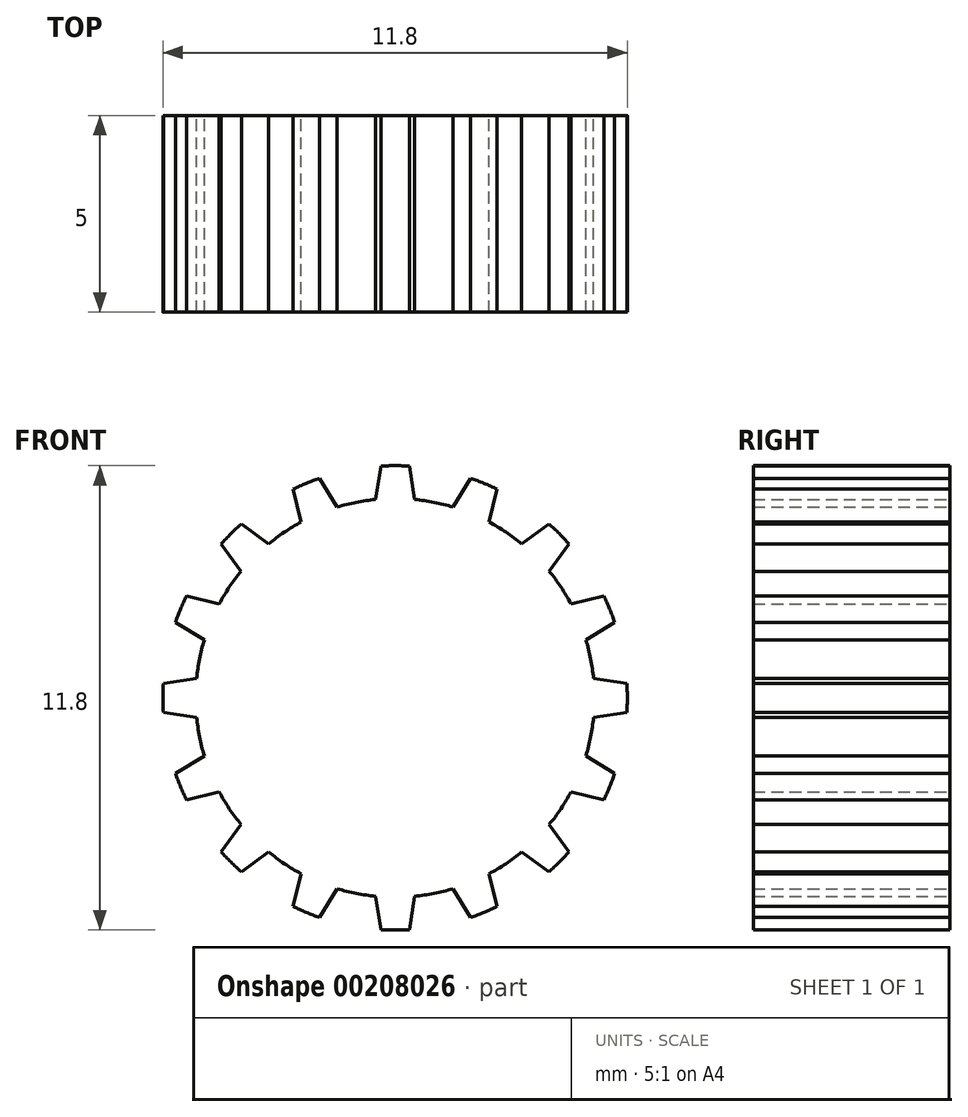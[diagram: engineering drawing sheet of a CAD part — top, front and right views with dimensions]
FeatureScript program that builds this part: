
annotation { "Feature Type Name" : "Feature", "Feature Type Description" : "" }
export const myFeature = defineFeature(function(context is Context, id is Id, definition is map)
    precondition{}
    {
        {
            var Q0;
            Q0=qCreatedBy(makeId("Front.planeOp"),FACE);
            var sketch = newSketch(context, id + "F0", { "sketchPlane" : qUnion([Q0])});
            skLineSegment(sketch, "E0", {"start": v(0, 0) * mm, "end": v(6.24, -1.24) * mm, "construction": true});
            skCircle(sketch, "E1", {"center": v(0, 0) * mm, "radius": 5.9 * mm, "construction": true});
            skCircle(sketch, "E2", {"center": v(0, 0) * mm, "radius": 5.07 * mm, "construction": true});
            skArc(sketch, "E3", {"start": v(4.97, -0.99) * mm, "mid": v(5.01, -0.74) * mm, "end": v(5.04, -0.5) * mm});
            skArc(sketch, "E4", {"start": v(5.9, 0) * mm, "mid": v(5.9, -0.18) * mm, "end": v(5.89, -0.36) * mm});
            skLineSegment(sketch, "E5", {"start": v(5.04, -0.5) * mm, "end": v(5.89, -0.36) * mm});
            skArc(sketch, "E6.MirrorCS", {"start": v(4.97, -0.99) * mm, "mid": v(4.91, -1.23) * mm, "end": v(4.85, -1.47) * mm});
            skLineSegment(sketch, "E7.MirrorCS", {"start": v(4.85, -1.47) * mm, "end": v(5.58, -1.92) * mm});
            skArc(sketch, "E8.MirrorCS", {"start": v(5.45, -2.26) * mm, "mid": v(5.52, -2.09) * mm, "end": v(5.58, -1.92) * mm});
            skArc(sketch, "E9.1.0", {"start": v(5.45, 2.26) * mm, "mid": v(5.52, 2.09) * mm, "end": v(5.58, 1.92) * mm});
            skLineSegment(sketch, "E9.1.1", {"start": v(4.85, 1.47) * mm, "end": v(5.58, 1.92) * mm});
            skArc(sketch, "E9.1.2", {"start": v(4.97, 0.99) * mm, "mid": v(4.91, 1.23) * mm, "end": v(4.85, 1.47) * mm});
            skArc(sketch, "E9.1.3", {"start": v(4.97, 0.99) * mm, "mid": v(5.01, 0.74) * mm, "end": v(5.04, 0.5) * mm});
            skLineSegment(sketch, "E9.1.4", {"start": v(5.04, 0.5) * mm, "end": v(5.89, 0.36) * mm});
            skArc(sketch, "E9.1.5", {"start": v(5.9, 0) * mm, "mid": v(5.9, 0.18) * mm, "end": v(5.89, 0.36) * mm});
            skArc(sketch, "E9.2.0", {"start": v(4.17, 4.17) * mm, "mid": v(4.3, 4.04) * mm, "end": v(4.42, 3.9) * mm});
            skLineSegment(sketch, "E9.2.1", {"start": v(3.91, 3.22) * mm, "end": v(4.42, 3.9) * mm});
            skArc(sketch, "E9.2.2", {"start": v(4.21, 2.81) * mm, "mid": v(4.07, 3.02) * mm, "end": v(3.91, 3.22) * mm});
            skArc(sketch, "E9.2.3", {"start": v(4.21, 2.81) * mm, "mid": v(4.35, 2.6) * mm, "end": v(4.47, 2.39) * mm});
            skLineSegment(sketch, "E9.2.4", {"start": v(4.47, 2.39) * mm, "end": v(5.3, 2.59) * mm});
            skArc(sketch, "E9.2.5", {"start": v(5.45, 2.26) * mm, "mid": v(5.38, 2.42) * mm, "end": v(5.3, 2.59) * mm});
            skArc(sketch, "E9.3.0", {"start": v(2.26, 5.45) * mm, "mid": v(2.42, 5.38) * mm, "end": v(2.59, 5.3) * mm});
            skLineSegment(sketch, "E9.3.1", {"start": v(2.39, 4.47) * mm, "end": v(2.59, 5.3) * mm});
            skArc(sketch, "E9.3.2", {"start": v(2.81, 4.21) * mm, "mid": v(2.6, 4.35) * mm, "end": v(2.39, 4.47) * mm});
            skArc(sketch, "E9.3.3", {"start": v(2.81, 4.21) * mm, "mid": v(3.02, 4.07) * mm, "end": v(3.22, 3.91) * mm});
            skLineSegment(sketch, "E9.3.4", {"start": v(3.22, 3.91) * mm, "end": v(3.9, 4.42) * mm});
            skArc(sketch, "E9.3.5", {"start": v(4.17, 4.17) * mm, "mid": v(4.04, 4.3) * mm, "end": v(3.9, 4.42) * mm});
            skArc(sketch, "E9.4.0", {"start": v(0, 5.9) * mm, "mid": v(0.18, 5.9) * mm, "end": v(0.36, 5.89) * mm});
            skLineSegment(sketch, "E9.4.1", {"start": v(0.5, 5.04) * mm, "end": v(0.36, 5.89) * mm});
            skArc(sketch, "E9.4.2", {"start": v(0.99, 4.97) * mm, "mid": v(0.74, 5.01) * mm, "end": v(0.5, 5.04) * mm});
            skArc(sketch, "E9.4.3", {"start": v(0.99, 4.97) * mm, "mid": v(1.23, 4.91) * mm, "end": v(1.47, 4.85) * mm});
            skLineSegment(sketch, "E9.4.4", {"start": v(1.47, 4.85) * mm, "end": v(1.92, 5.58) * mm});
            skArc(sketch, "E9.4.5", {"start": v(2.26, 5.45) * mm, "mid": v(2.09, 5.52) * mm, "end": v(1.92, 5.58) * mm});
            skArc(sketch, "E9.5.0", {"start": v(-2.26, 5.45) * mm, "mid": v(-2.09, 5.52) * mm, "end": v(-1.92, 5.58) * mm});
            skLineSegment(sketch, "E9.5.1", {"start": v(-1.47, 4.85) * mm, "end": v(-1.92, 5.58) * mm});
            skArc(sketch, "E9.5.2", {"start": v(-0.99, 4.97) * mm, "mid": v(-1.23, 4.91) * mm, "end": v(-1.47, 4.85) * mm});
            skArc(sketch, "E9.5.3", {"start": v(-0.99, 4.97) * mm, "mid": v(-0.74, 5.01) * mm, "end": v(-0.5, 5.04) * mm});
            skLineSegment(sketch, "E9.5.4", {"start": v(-0.5, 5.04) * mm, "end": v(-0.36, 5.89) * mm});
            skArc(sketch, "E9.5.5", {"start": v(0, 5.9) * mm, "mid": v(-0.18, 5.9) * mm, "end": v(-0.36, 5.89) * mm});
            skArc(sketch, "E9.6.0", {"start": v(-4.17, 4.17) * mm, "mid": v(-4.04, 4.3) * mm, "end": v(-3.9, 4.42) * mm});
            skLineSegment(sketch, "E9.6.1", {"start": v(-3.22, 3.91) * mm, "end": v(-3.9, 4.42) * mm});
            skArc(sketch, "E9.6.2", {"start": v(-2.81, 4.21) * mm, "mid": v(-3.02, 4.07) * mm, "end": v(-3.22, 3.91) * mm});
            skArc(sketch, "E9.6.3", {"start": v(-2.81, 4.21) * mm, "mid": v(-2.6, 4.35) * mm, "end": v(-2.39, 4.47) * mm});
            skLineSegment(sketch, "E9.6.4", {"start": v(-2.39, 4.47) * mm, "end": v(-2.59, 5.3) * mm});
            skArc(sketch, "E9.6.5", {"start": v(-2.26, 5.45) * mm, "mid": v(-2.42, 5.38) * mm, "end": v(-2.59, 5.3) * mm});
            skArc(sketch, "E9.7.0", {"start": v(-5.45, 2.26) * mm, "mid": v(-5.38, 2.42) * mm, "end": v(-5.3, 2.59) * mm});
            skLineSegment(sketch, "E9.7.1", {"start": v(-4.47, 2.39) * mm, "end": v(-5.3, 2.59) * mm});
            skArc(sketch, "E9.7.2", {"start": v(-4.21, 2.81) * mm, "mid": v(-4.35, 2.6) * mm, "end": v(-4.47, 2.39) * mm});
            skArc(sketch, "E9.7.3", {"start": v(-4.21, 2.81) * mm, "mid": v(-4.07, 3.02) * mm, "end": v(-3.91, 3.22) * mm});
            skLineSegment(sketch, "E9.7.4", {"start": v(-3.91, 3.22) * mm, "end": v(-4.42, 3.9) * mm});
            skArc(sketch, "E9.7.5", {"start": v(-4.17, 4.17) * mm, "mid": v(-4.3, 4.04) * mm, "end": v(-4.42, 3.9) * mm});
            skArc(sketch, "E9.8.0", {"start": v(-5.9, 0) * mm, "mid": v(-5.9, 0.18) * mm, "end": v(-5.89, 0.36) * mm});
            skLineSegment(sketch, "E9.8.1", {"start": v(-5.04, 0.5) * mm, "end": v(-5.89, 0.36) * mm});
            skArc(sketch, "E9.8.2", {"start": v(-4.97, 0.99) * mm, "mid": v(-5.01, 0.74) * mm, "end": v(-5.04, 0.5) * mm});
            skArc(sketch, "E9.8.3", {"start": v(-4.97, 0.99) * mm, "mid": v(-4.91, 1.23) * mm, "end": v(-4.85, 1.47) * mm});
            skLineSegment(sketch, "E9.8.4", {"start": v(-4.85, 1.47) * mm, "end": v(-5.58, 1.92) * mm});
            skArc(sketch, "E9.8.5", {"start": v(-5.45, 2.26) * mm, "mid": v(-5.52, 2.09) * mm, "end": v(-5.58, 1.92) * mm});
            skArc(sketch, "E9.9.0", {"start": v(-5.45, -2.26) * mm, "mid": v(-5.52, -2.09) * mm, "end": v(-5.58, -1.92) * mm});
            skLineSegment(sketch, "E9.9.1", {"start": v(-4.85, -1.47) * mm, "end": v(-5.58, -1.92) * mm});
            skArc(sketch, "E9.9.2", {"start": v(-4.97, -0.99) * mm, "mid": v(-4.91, -1.23) * mm, "end": v(-4.85, -1.47) * mm});
            skArc(sketch, "E9.9.3", {"start": v(-4.97, -0.99) * mm, "mid": v(-5.01, -0.74) * mm, "end": v(-5.04, -0.5) * mm});
            skLineSegment(sketch, "E9.9.4", {"start": v(-5.04, -0.5) * mm, "end": v(-5.89, -0.36) * mm});
            skArc(sketch, "E9.9.5", {"start": v(-5.9, 0) * mm, "mid": v(-5.9, -0.18) * mm, "end": v(-5.89, -0.36) * mm});
            skArc(sketch, "E9.10.0", {"start": v(-4.17, -4.17) * mm, "mid": v(-4.3, -4.04) * mm, "end": v(-4.42, -3.9) * mm});
            skLineSegment(sketch, "E9.10.1", {"start": v(-3.91, -3.22) * mm, "end": v(-4.42, -3.9) * mm});
            skArc(sketch, "E9.10.2", {"start": v(-4.21, -2.81) * mm, "mid": v(-4.07, -3.02) * mm, "end": v(-3.91, -3.22) * mm});
            skArc(sketch, "E9.10.3", {"start": v(-4.21, -2.81) * mm, "mid": v(-4.35, -2.6) * mm, "end": v(-4.47, -2.39) * mm});
            skLineSegment(sketch, "E9.10.4", {"start": v(-4.47, -2.39) * mm, "end": v(-5.3, -2.59) * mm});
            skArc(sketch, "E9.10.5", {"start": v(-5.45, -2.26) * mm, "mid": v(-5.38, -2.42) * mm, "end": v(-5.3, -2.59) * mm});
            skArc(sketch, "E9.11.0", {"start": v(-2.26, -5.45) * mm, "mid": v(-2.42, -5.38) * mm, "end": v(-2.59, -5.3) * mm});
            skLineSegment(sketch, "E9.11.1", {"start": v(-2.39, -4.47) * mm, "end": v(-2.59, -5.3) * mm});
            skArc(sketch, "E9.11.2", {"start": v(-2.81, -4.21) * mm, "mid": v(-2.6, -4.35) * mm, "end": v(-2.39, -4.47) * mm});
            skArc(sketch, "E9.11.3", {"start": v(-2.81, -4.21) * mm, "mid": v(-3.02, -4.07) * mm, "end": v(-3.22, -3.91) * mm});
            skLineSegment(sketch, "E9.11.4", {"start": v(-3.22, -3.91) * mm, "end": v(-3.9, -4.42) * mm});
            skArc(sketch, "E9.11.5", {"start": v(-4.17, -4.17) * mm, "mid": v(-4.04, -4.3) * mm, "end": v(-3.9, -4.42) * mm});
            skArc(sketch, "E9.12.0", {"start": v(0, -5.9) * mm, "mid": v(-0.18, -5.9) * mm, "end": v(-0.36, -5.89) * mm});
            skLineSegment(sketch, "E9.12.1", {"start": v(-0.5, -5.04) * mm, "end": v(-0.36, -5.89) * mm});
            skArc(sketch, "E9.12.2", {"start": v(-0.99, -4.97) * mm, "mid": v(-0.74, -5.01) * mm, "end": v(-0.5, -5.04) * mm});
            skArc(sketch, "E9.12.3", {"start": v(-0.99, -4.97) * mm, "mid": v(-1.23, -4.91) * mm, "end": v(-1.47, -4.85) * mm});
            skLineSegment(sketch, "E9.12.4", {"start": v(-1.47, -4.85) * mm, "end": v(-1.92, -5.58) * mm});
            skArc(sketch, "E9.12.5", {"start": v(-2.26, -5.45) * mm, "mid": v(-2.09, -5.52) * mm, "end": v(-1.92, -5.58) * mm});
            skArc(sketch, "E9.13.0", {"start": v(2.26, -5.45) * mm, "mid": v(2.09, -5.52) * mm, "end": v(1.92, -5.58) * mm});
            skLineSegment(sketch, "E9.13.1", {"start": v(1.47, -4.85) * mm, "end": v(1.92, -5.58) * mm});
            skArc(sketch, "E9.13.2", {"start": v(0.99, -4.97) * mm, "mid": v(1.23, -4.91) * mm, "end": v(1.47, -4.85) * mm});
            skArc(sketch, "E9.13.3", {"start": v(0.99, -4.97) * mm, "mid": v(0.74, -5.01) * mm, "end": v(0.5, -5.04) * mm});
            skLineSegment(sketch, "E9.13.4", {"start": v(0.5, -5.04) * mm, "end": v(0.36, -5.89) * mm});
            skArc(sketch, "E9.13.5", {"start": v(0, -5.9) * mm, "mid": v(0.18, -5.9) * mm, "end": v(0.36, -5.89) * mm});
            skArc(sketch, "E9.14.0", {"start": v(4.17, -4.17) * mm, "mid": v(4.04, -4.3) * mm, "end": v(3.9, -4.42) * mm});
            skLineSegment(sketch, "E9.14.1", {"start": v(3.22, -3.91) * mm, "end": v(3.9, -4.42) * mm});
            skArc(sketch, "E9.14.2", {"start": v(2.81, -4.21) * mm, "mid": v(3.02, -4.07) * mm, "end": v(3.22, -3.91) * mm});
            skArc(sketch, "E9.14.3", {"start": v(2.81, -4.21) * mm, "mid": v(2.6, -4.35) * mm, "end": v(2.39, -4.47) * mm});
            skLineSegment(sketch, "E9.14.4", {"start": v(2.39, -4.47) * mm, "end": v(2.59, -5.3) * mm});
            skArc(sketch, "E9.14.5", {"start": v(2.26, -5.45) * mm, "mid": v(2.42, -5.38) * mm, "end": v(2.59, -5.3) * mm});
            skArc(sketch, "E9.15.0", {"start": v(5.45, -2.26) * mm, "mid": v(5.38, -2.42) * mm, "end": v(5.3, -2.59) * mm});
            skLineSegment(sketch, "E9.15.1", {"start": v(4.47, -2.39) * mm, "end": v(5.3, -2.59) * mm});
            skArc(sketch, "E9.15.2", {"start": v(4.21, -2.81) * mm, "mid": v(4.35, -2.6) * mm, "end": v(4.47, -2.39) * mm});
            skArc(sketch, "E9.15.3", {"start": v(4.21, -2.81) * mm, "mid": v(4.07, -3.02) * mm, "end": v(3.91, -3.22) * mm});
            skLineSegment(sketch, "E9.15.4", {"start": v(3.91, -3.22) * mm, "end": v(4.42, -3.9) * mm});
            skArc(sketch, "E9.15.5", {"start": v(4.17, -4.17) * mm, "mid": v(4.3, -4.04) * mm, "end": v(4.42, -3.9) * mm});
            skSolve(sketch);
        }
        {
            var Q0;
            Q0=makeQuery(id+"F0.imprint","IMPRINT",FACE,{"disambiguationData":[TD([[makeQuery(id+"F0.imprint","IMPRINT",EDGE,{"derivedFrom":sQuery(id+"F0.wireOp",EDGE,"E3")}),1.0]])]});
            extrude(context, id + "F1", {"entities" : qUnion([Q0]), "depth" : 5 * mm});
        }
    });
